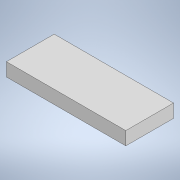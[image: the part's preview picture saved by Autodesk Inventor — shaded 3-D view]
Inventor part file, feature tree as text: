
AUTODESK INVENTOR PART (.ipt)
format: ipt  version: 2020 (Build 240168000, 168)  size: 89,088 bytes
history: native  units: mm
features: extrude x1, sketch x1
ambient origin geometry x8: Origin, YZ Plane, XZ Plane, XY Plane, X Axis, Y Axis, Z Axis, Center Point
bodies: Solid1 (feature_tree)
feature tree (2):
  extrude  "Extrusion1"  Depth=18.0mm
  sketch  "Sketch1"  dims[d0=45.0mm d1=18.0mm d2=5.0mm d3=0.0mm]
